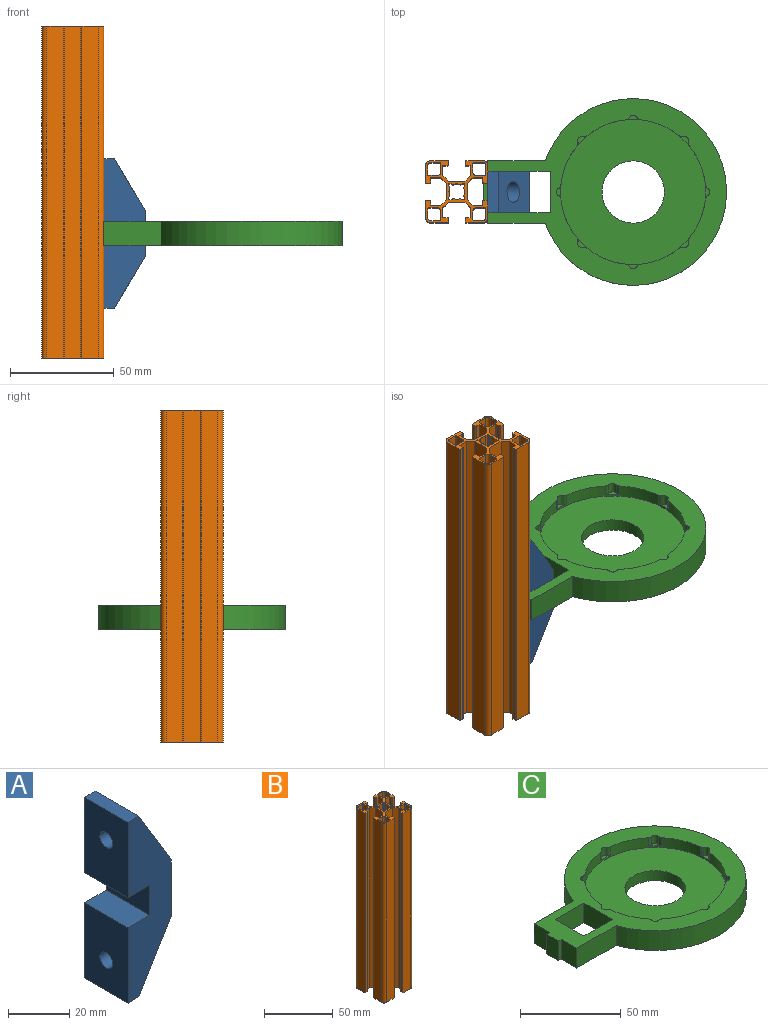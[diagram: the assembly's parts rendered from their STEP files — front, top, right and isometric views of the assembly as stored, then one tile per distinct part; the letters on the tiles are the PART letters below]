
ASSEMBLY  parts=3 mates=2
PART A: 18 faces, bbox 20x20x72 mm
  f0: cylinder r=3mm len=6.8mm, axis (1,0,0), area 128.1mm2, adj f4,f10
  f1: plane 72x20mm, normal (0,1,0), area 945mm2, adj f2,f3,f4,f5,f6,f7,f12,f13
  f2: plane 25x20mm, normal (0.86,0,0.51), area 491.5mm2, adj f1,f3,f7,f8,f9
  f3: plane 20x5mm, normal (0,0,1), area 100mm2, adj f1,f2,f4,f8
  f4: plane 30x20mm, normal (-1,0,0), area 571.7mm2, adj f0,f1,f3,f5,f8
  f5: plane 20x10mm, normal (0,0,-1), area 200mm2, adj f1,f4,f6,f8
  f6: plane 20x12mm, normal (-1,0,0), area 240mm2, adj f1,f5,f8,f15
  f7: plane 22x20mm, normal (1,0,0), area 440mm2, adj f1,f2,f8,f12
  f8: plane 72x20mm, normal (0,-1,0), area 945mm2, adj f2,f3,f4,f5,f6,f7,f12,f13
  f9: cylinder r=5mm len=10mm, axis (1,0,0), area 131.9mm2, adj f2,f10
  f10: cone r=0mm half-angle=59deg, axis (1,0,0), area 58.6mm2, adj f0,f9
  f11: cylinder r=3mm len=6.8mm, axis (1,0,0), area 128.1mm2, adj f14,f17
  f12: plane 25x20mm, normal (0.86,0,-0.51), area 491.5mm2, adj f1,f7,f8,f13,f16
  f13: plane 20x5mm, normal (0,0,-1), area 100mm2, adj f1,f8,f12,f14
  f14: plane 30x20mm, normal (-1,0,0), area 571.7mm2, adj f1,f8,f11,f13,f15
  f15: plane 20x10mm, normal (0,0,1), area 200mm2, adj f1,f6,f8,f14
  f16: cylinder r=5mm len=10mm, axis (1,0,0), area 131.9mm2, adj f12,f17
  f17: cone r=0mm half-angle=59deg, axis (1,0,0), area 58.6mm2, adj f11,f16
PART B: 138 faces, bbox 30x30x160 mm
  f0: cylinder r=0.5mm len=160mm, axis (0,0,-1), area 125.7mm2, adj f1,f135,f136,f137
  f1: plane 160x4.2mm, normal (0,-1,0), area 672mm2, adj f0,f2,f136,f137
  f2: cylinder r=1.5mm len=160mm, axis (0,0,-1), area 377mm2, adj f1,f3,f136,f137
  f3: plane 160x4.2mm, normal (-1,0,0), area 672mm2, adj f2,f4,f136,f137
  f4: cylinder r=0.5mm len=160mm, axis (0,0,-1), area 125.7mm2, adj f3,f5,f136,f137
  f5: plane 160x4.2mm, normal (0,1,0), area 672mm2, adj f4,f6,f136,f137
  f6: cylinder r=1.5mm len=160mm, axis (0,0,-1), area 377mm2, adj f5,f135,f136,f137
  f7: cylinder r=1.5mm len=160mm, axis (0,0,-1), area 377mm2, adj f8,f130,f136,f137
  f8: plane 160x4.2mm, normal (0,-1,0), area 672mm2, adj f7,f9,f136,f137
  f9: cylinder r=0.5mm len=160mm, axis (0,0,-1), area 125.7mm2, adj f8,f10,f136,f137
  f10: plane 160x4.2mm, normal (-1,0,0), area 672mm2, adj f9,f11,f136,f137
  f11: cylinder r=1.5mm len=160mm, axis (0,0,-1), area 377mm2, adj f10,f12,f136,f137
  f12: plane 160x4.2mm, normal (0,1,0), area 672mm2, adj f11,f13,f136,f137
  f13: cylinder r=0.5mm len=160mm, axis (0,0,-1), area 125.7mm2, adj f12,f130,f136,f137
  f14: cylinder r=0.5mm len=160mm, axis (0,0,-1), area 125.7mm2, adj f15,f131,f136,f137
  f15: plane 160x4.2mm, normal (0,-1,0), area 672mm2, adj f14,f16,f136,f137
  f16: cylinder r=1.5mm len=160mm, axis (0,0,-1), area 377mm2, adj f15,f17,f136,f137
  f17: plane 160x4.2mm, normal (-1,0,0), area 672mm2, adj f16,f18,f136,f137
  f18: cylinder r=0.5mm len=160mm, axis (0,0,-1), area 125.7mm2, adj f17,f19,f136,f137
  f19: plane 160x4.2mm, normal (0,1,0), area 672mm2, adj f18,f20,f136,f137
  f20: cylinder r=1.5mm len=160mm, axis (0,0,-1), area 377mm2, adj f19,f131,f136,f137
  f21: cylinder r=1.5mm len=160mm, axis (0,0,-1), area 377mm2, adj f22,f132,f136,f137
  f22: plane 160x4.2mm, normal (0,-1,0), area 672mm2, adj f21,f23,f136,f137
  f23: cylinder r=0.5mm len=160mm, axis (0,0,-1), area 125.7mm2, adj f22,f24,f136,f137
  f24: plane 160x4.2mm, normal (-1,0,0), area 672mm2, adj f23,f25,f136,f137
  f25: cylinder r=1.5mm len=160mm, axis (0,0,-1), area 377mm2, adj f24,f26,f136,f137
  f26: plane 160x4.2mm, normal (0,1,0), area 672mm2, adj f25,f27,f136,f137
  f27: cylinder r=0.5mm len=160mm, axis (0,0,-1), area 125.7mm2, adj f26,f132,f136,f137
  f28: plane 160x0.24mm, normal (0.71,-0.71,0), area 53.8mm2, adj f29,f133,f136,f137
  f29: cylinder r=0.3mm len=160mm, axis (0,0,-1), area 59.7mm2, adj f28,f30,f136,f137
  f30: cylinder r=3.75mm len=160mm, axis (0,0,-1), area 550.4mm2, adj f29,f31,f136,f137
  f31: cylinder r=0.3mm len=160mm, axis (0,0,-1), area 59.7mm2, adj f30,f32,f136,f137
  f32: plane 160x0.24mm, normal (0.71,0.71,0), area 53.8mm2, adj f31,f33,f136,f137
  f33: plane 160x1.04mm, normal (0.98,0.21,0), area 170.6mm2, adj f32,f34,f136,f137
  f34: cylinder r=0.5mm len=160mm, axis (0,0,-1), area 159.2mm2, adj f33,f35,f136,f137
  f35: plane 160x1.04mm, normal (-0.21,-0.98,0), area 170.6mm2, adj f34,f36,f136,f137
  f36: plane 160x0.24mm, normal (-0.71,-0.71,0), area 53.8mm2, adj f35,f37,f136,f137
  f37: cylinder r=0.3mm len=160mm, axis (0,0,-1), area 59.7mm2, adj f36,f38,f136,f137
  f38: cylinder r=3.75mm len=160mm, axis (0,0,-1), area 550.4mm2, adj f37,f39,f136,f137
  f39: cylinder r=0.3mm len=160mm, axis (0,0,-1), area 59.7mm2, adj f38,f40,f136,f137
  f40: plane 160x0.24mm, normal (0.71,-0.71,0), area 53.8mm2, adj f39,f41,f136,f137
  f41: plane 160x1.04mm, normal (0.21,-0.98,0), area 170.6mm2, adj f40,f42,f136,f137
  f42: cylinder r=0.5mm len=160mm, axis (0,0,-1), area 159.2mm2, adj f41,f43,f136,f137
  f43: plane 160x1.04mm, normal (-0.98,0.21,0), area 170.6mm2, adj f42,f44,f136,f137
  f44: plane 160x0.24mm, normal (-0.71,0.71,0), area 53.8mm2, adj f43,f45,f136,f137
  f45: cylinder r=0.3mm len=160mm, axis (0,0,-1), area 59.7mm2, adj f44,f46,f136,f137
  f46: cylinder r=3.75mm len=160mm, axis (0,0,-1), area 550.4mm2, adj f45,f47,f136,f137
  f47: cylinder r=0.3mm len=160mm, axis (0,0,-1), area 59.7mm2, adj f46,f48,f136,f137
  f48: plane 160x0.24mm, normal (-0.71,-0.71,0), area 53.8mm2, adj f47,f49,f136,f137
  f49: plane 160x1.04mm, normal (-0.98,-0.21,0), area 170.6mm2, adj f48,f50,f136,f137
  f50: cylinder r=0.5mm len=160mm, axis (0,0,-1), area 159.2mm2, adj f49,f51,f136,f137
  f51: plane 160x1.04mm, normal (0.21,0.98,0), area 170.6mm2, adj f50,f52,f136,f137
  f52: plane 160x0.24mm, normal (0.71,0.71,0), area 53.8mm2, adj f51,f53,f136,f137
  f53: cylinder r=0.3mm len=160mm, axis (0,0,-1), area 59.7mm2, adj f52,f54,f136,f137
  f54: cylinder r=3.75mm len=160mm, axis (0,0,-1), area 550.4mm2, adj f53,f55,f136,f137
  f55: cylinder r=0.3mm len=160mm, axis (0,0,-1), area 59.7mm2, adj f54,f56,f136,f137
  f56: plane 160x0.24mm, normal (-0.71,0.71,0), area 53.8mm2, adj f55,f57,f136,f137
  f57: plane 160x1.04mm, normal (-0.21,0.98,0), area 170.6mm2, adj f56,f58,f136,f137
  f58: cylinder r=0.5mm len=160mm, axis (0,0,-1), area 159.2mm2, adj f57,f133,f136,f137
  f59: cylinder r=0.3mm len=160mm, axis (0,0,-1), area 75.4mm2, adj f60,f134,f136,f137
  f60: plane 160x4.34mm, normal (-1,0,0), area 694.3mm2, adj f59,f61,f136,f137
  f61: plane 160x2.86mm, normal (-0.71,0.71,0), area 647.3mm2, adj f60,f62,f136,f137
  f62: plane 160x7.88mm, normal (0,1,0), area 1260.6mm2, adj f61,f63,f136,f137
  f63: plane 160x2.86mm, normal (0.71,0.71,0), area 647.3mm2, adj f62,f64,f136,f137
  f64: plane 160x4.34mm, normal (1,0,0), area 694.3mm2, adj f63,f65,f136,f137
  f65: cylinder r=0.3mm len=160mm, axis (0,0,-1), area 75.4mm2, adj f64,f66,f136,f137
  f66: plane 160x1.9mm, normal (0,-1,0), area 304mm2, adj f65,f67,f136,f137
  f67: cylinder r=0.5mm len=160mm, axis (0,0,-1), area 125.7mm2, adj f66,f68,f136,f137
  f68: plane 160x1.7mm, normal (1,0,0), area 272mm2, adj f67,f69,f136,f137
  f69: cylinder r=0.3mm len=160mm, axis (0,0,-1), area 75.4mm2, adj f68,f70,f136,f137
  f70: plane 160x8.1mm, normal (0,1,0), area 1296mm2, adj f69,f71,f136,f137
  f71: cylinder r=2.5mm len=160mm, axis (0,0,-1), area 628.3mm2, adj f70,f72,f136,f137
  f72: plane 160x8.1mm, normal (-1,0,0), area 1296mm2, adj f71,f73,f136,f137
  f73: cylinder r=0.3mm len=160mm, axis (0,0,-1), area 75.4mm2, adj f72,f74,f136,f137
  f74: plane 160x1.7mm, normal (0,-1,0), area 272mm2, adj f73,f75,f136,f137
  f75: cylinder r=0.5mm len=160mm, axis (0,0,-1), area 125.7mm2, adj f74,f76,f136,f137
  f76: plane 160x1.9mm, normal (1,0,0), area 304mm2, adj f75,f77,f136,f137
  f77: cylinder r=0.3mm len=160mm, axis (0,0,-1), area 75.4mm2, adj f76,f78,f136,f137
  f78: plane 160x4.34mm, normal (0,-1,0), area 694.3mm2, adj f77,f79,f136,f137
  f79: plane 160x2.86mm, normal (-0.71,-0.71,0), area 647.3mm2, adj f78,f80,f136,f137
  f80: plane 160x7.88mm, normal (-1,0,0), area 1260.6mm2, adj f79,f81,f136,f137
  f81: plane 160x2.86mm, normal (-0.71,0.71,0), area 647.3mm2, adj f80,f82,f136,f137
  f82: plane 160x4.34mm, normal (0,1,0), area 694.3mm2, adj f81,f83,f136,f137
  f83: cylinder r=0.3mm len=160mm, axis (0,0,-1), area 75.4mm2, adj f82,f84,f136,f137
  f84: plane 160x1.9mm, normal (1,0,0), area 304mm2, adj f83,f85,f136,f137
  f85: cylinder r=0.5mm len=160mm, axis (0,0,-1), area 125.7mm2, adj f84,f86,f136,f137
  f86: plane 160x1.7mm, normal (0,1,0), area 272mm2, adj f85,f87,f136,f137
  f87: cylinder r=0.3mm len=160mm, axis (0,0,-1), area 75.4mm2, adj f86,f88,f136,f137
  f88: plane 160x8.1mm, normal (-1,0,0), area 1296mm2, adj f87,f89,f136,f137
  f89: cylinder r=2.5mm len=160mm, axis (0,0,-1), area 628.3mm2, adj f88,f90,f136,f137
  f90: plane 160x8.1mm, normal (0,-1,0), area 1296mm2, adj f89,f91,f136,f137
  f91: cylinder r=0.3mm len=160mm, axis (0,0,-1), area 75.4mm2, adj f90,f92,f136,f137
  f92: plane 160x1.7mm, normal (1,0,0), area 272mm2, adj f91,f93,f136,f137
  f93: cylinder r=0.5mm len=160mm, axis (0,0,-1), area 125.7mm2, adj f92,f94,f136,f137
  f94: plane 160x1.9mm, normal (0,1,0), area 304mm2, adj f93,f95,f136,f137
  f95: cylinder r=0.3mm len=160mm, axis (0,0,-1), area 75.4mm2, adj f94,f96,f136,f137
  f96: plane 160x4.34mm, normal (1,0,0), area 694.3mm2, adj f95,f97,f136,f137
  f97: plane 160x2.86mm, normal (0.71,-0.71,0), area 647.3mm2, adj f96,f98,f136,f137
  f98: plane 160x7.88mm, normal (0,-1,0), area 1260.6mm2, adj f97,f99,f136,f137
  f99: plane 160x2.86mm, normal (-0.71,-0.71,0), area 647.3mm2, adj f98,f100,f136,f137
  f100: plane 160x4.34mm, normal (-1,0,0), area 694.3mm2, adj f99,f101,f136,f137
  f101: cylinder r=0.3mm len=160mm, axis (0,0,-1), area 75.4mm2, adj f100,f102,f136,f137
  f102: plane 160x1.9mm, normal (0,1,0), area 304mm2, adj f101,f103,f136,f137
  f103: cylinder r=0.5mm len=160mm, axis (0,0,-1), area 125.7mm2, adj f102,f104,f136,f137
  f104: plane 160x1.7mm, normal (-1,0,0), area 272mm2, adj f103,f105,f136,f137
  f105: cylinder r=0.3mm len=160mm, axis (0,0,-1), area 75.4mm2, adj f104,f106,f136,f137
  f106: plane 160x8.1mm, normal (0,-1,0), area 1296mm2, adj f105,f107,f136,f137
  f107: cylinder r=2.5mm len=160mm, axis (0,0,-1), area 628.3mm2, adj f106,f108,f136,f137
  f108: plane 160x8.1mm, normal (1,0,0), area 1296mm2, adj f107,f109,f136,f137
  f109: cylinder r=0.3mm len=160mm, axis (0,0,-1), area 75.4mm2, adj f108,f110,f136,f137
  f110: plane 160x1.7mm, normal (0,1,0), area 272mm2, adj f109,f111,f136,f137
  f111: cylinder r=0.5mm len=160mm, axis (0,0,-1), area 125.7mm2, adj f110,f112,f136,f137
  f112: plane 160x1.9mm, normal (-1,0,0), area 304mm2, adj f111,f113,f136,f137
  f113: cylinder r=0.3mm len=160mm, axis (0,0,-1), area 75.4mm2, adj f112,f114,f136,f137
  f114: plane 160x4.34mm, normal (0,1,0), area 694.3mm2, adj f113,f115,f136,f137
  f115: plane 160x2.86mm, normal (0.71,0.71,0), area 647.3mm2, adj f114,f116,f136,f137
  f116: plane 160x7.88mm, normal (1,0,0), area 1260.6mm2, adj f115,f117,f136,f137
  f117: plane 160x2.86mm, normal (0.71,-0.71,0), area 647.3mm2, adj f116,f118,f136,f137
  f118: plane 160x4.34mm, normal (0,-1,0), area 694.3mm2, adj f117,f119,f136,f137
  f119: cylinder r=0.3mm len=160mm, axis (0,0,-1), area 75.4mm2, adj f118,f120,f136,f137
  f120: plane 160x1.9mm, normal (-1,0,0), area 304mm2, adj f119,f121,f136,f137
  f121: cylinder r=0.5mm len=160mm, axis (0,0,-1), area 125.7mm2, adj f120,f122,f136,f137
  f122: plane 160x1.7mm, normal (0,-1,0), area 272mm2, adj f121,f123,f136,f137
  f123: cylinder r=0.3mm len=160mm, axis (0,0,-1), area 75.4mm2, adj f122,f124,f136,f137
  f124: plane 160x8.1mm, normal (1,0,0), area 1296mm2, adj f123,f125,f136,f137
  f125: cylinder r=2.5mm len=160mm, axis (0,0,-1), area 628.3mm2, adj f124,f126,f136,f137
  f126: plane 160x8.1mm, normal (0,1,0), area 1296mm2, adj f125,f127,f136,f137
  f127: cylinder r=0.3mm len=160mm, axis (0,0,-1), area 75.4mm2, adj f126,f128,f136,f137
  f128: plane 160x1.7mm, normal (-1,0,0), area 272mm2, adj f127,f129,f136,f137
  f129: cylinder r=0.5mm len=160mm, axis (0,0,-1), area 125.7mm2, adj f128,f134,f136,f137
  f130: plane 160x4.2mm, normal (1,0,0), area 672mm2, adj f7,f13,f136,f137
  f131: plane 160x4.2mm, normal (1,0,0), area 672mm2, adj f14,f20,f136,f137
  f132: plane 160x4.2mm, normal (1,0,0), area 672mm2, adj f21,f27,f136,f137
  f133: plane 160x1.04mm, normal (0.98,-0.21,0), area 170.6mm2, adj f28,f58,f136,f137
  f134: plane 160x1.9mm, normal (0,-1,0), area 304mm2, adj f59,f129,f136,f137
  f135: plane 160x4.2mm, normal (1,0,0), area 672mm2, adj f0,f6,f136,f137
  f136: plane 30x30mm, normal (0,0,1), area 233.9mm2, adj f0,f1,f2,f3,f4,f5,f6,f7
  f137: plane 30x30mm, normal (0,0,-1), area 233.9mm2, adj f0,f1,f2,f3,f4,f5,f6,f7
PART C: 49 faces, bbox 117x90x12 mm
  f0: plane 12x10.9mm, normal (-1,0,0), area 130.8mm2, adj f1,f2,f7,f46
  f1: plane 117x90mm, normal (0,0,-1), area 6046.7mm2, adj f0,f3,f6,f7,f8,f9,f42,f43
  f2: plane 117x90mm, normal (0,0,1), area 2849.6mm2, adj f0,f5,f6,f7,f8,f9,f10,f12
  f3: cylinder r=15mm len=30mm, axis (0,0,-1), area 565.5mm2, adj f1,f4
  f4: plane 70x70mm, normal (0,0,1), area 3141.6mm2, adj f3,f5
  f5: cylinder r=35mm len=70mm, axis (0,0,-1), area 1049.8mm2, adj f2,f4,f11,f12,f13,f15,f16,f17
  f6: cylinder r=45mm len=90mm, axis (0,0,-1), area 3025.9mm2, adj f1,f2,f7,f9
  f7: plane 27.57x12mm, normal (0,1,0), area 330.9mm2, adj f0,f1,f2,f6
  f8: plane 12x10.9mm, normal (-1,0,0), area 130.8mm2, adj f1,f2,f9,f47
  f9: plane 27.57x12mm, normal (0,-1,0), area 330.9mm2, adj f1,f2,f6,f8
  f10: cylinder r=2mm len=5mm, axis (0,0,1), area 21.9mm2, adj f2,f11,f12,f13
  f11: plane 6.73x2.16mm, normal (0,0,1), area 6.9mm2, adj f5,f10,f12,f13
  f12: cylinder r=2mm len=5mm, axis (0,0,1), area 10mm2, adj f2,f5,f10,f11
  f13: cylinder r=2mm len=5mm, axis (0,0,-1), area 10mm2, adj f2,f5,f10,f11
  f14: cylinder r=2mm len=5mm, axis (0,0,1), area 21.9mm2, adj f2,f15,f16,f17
  f15: plane 4.76x4.76mm, normal (0,0,1), area 6.9mm2, adj f5,f14,f16,f17
  f16: cylinder r=2mm len=5mm, axis (0,0,1), area 10mm2, adj f2,f5,f14,f15
  f17: cylinder r=2mm len=5mm, axis (0,0,-1), area 10mm2, adj f2,f5,f14,f15
  f18: cylinder r=2mm len=5mm, axis (0,0,1), area 21.9mm2, adj f2,f19,f20,f21
  f19: plane 6.73x2.16mm, normal (0,0,1), area 6.9mm2, adj f5,f18,f20,f21
  f20: cylinder r=2mm len=5mm, axis (0,0,1), area 10mm2, adj f2,f5,f18,f19
  f21: cylinder r=2mm len=5mm, axis (0,0,-1), area 10mm2, adj f2,f5,f18,f19
  f22: cylinder r=2mm len=5mm, axis (0,0,1), area 21.9mm2, adj f2,f23,f24,f25
  f23: plane 4.76x4.76mm, normal (0,0,1), area 6.9mm2, adj f5,f22,f24,f25
  f24: cylinder r=2mm len=5mm, axis (0,0,1), area 10mm2, adj f2,f5,f22,f23
  f25: cylinder r=2mm len=5mm, axis (0,0,-1), area 10mm2, adj f2,f5,f22,f23
  f26: cylinder r=2mm len=5mm, axis (0,0,1), area 21.9mm2, adj f2,f27,f28,f29
  f27: plane 6.73x2.16mm, normal (0,0,1), area 6.9mm2, adj f5,f26,f28,f29
  f28: cylinder r=2mm len=5mm, axis (0,0,1), area 10mm2, adj f2,f5,f26,f27
  f29: cylinder r=2mm len=5mm, axis (0,0,-1), area 10mm2, adj f2,f5,f26,f27
  f30: cylinder r=2mm len=5mm, axis (0,0,1), area 21.9mm2, adj f2,f31,f32,f33
  f31: plane 4.76x4.76mm, normal (0,0,1), area 6.9mm2, adj f5,f30,f32,f33
  f32: cylinder r=2mm len=5mm, axis (0,0,1), area 10mm2, adj f2,f5,f30,f31
  f33: cylinder r=2mm len=5mm, axis (0,0,-1), area 10mm2, adj f2,f5,f30,f31
  f34: cylinder r=2mm len=5mm, axis (0,0,1), area 21.9mm2, adj f2,f35,f36,f37
  f35: plane 6.73x2.16mm, normal (0,0,1), area 6.9mm2, adj f5,f34,f36,f37
  f36: cylinder r=2mm len=5mm, axis (0,0,1), area 10mm2, adj f2,f5,f34,f35
  f37: cylinder r=2mm len=5mm, axis (0,0,-1), area 10mm2, adj f2,f5,f34,f35
  f38: cylinder r=2mm len=5mm, axis (0,0,1), area 21.9mm2, adj f2,f39,f40,f41
  f39: plane 4.76x4.76mm, normal (0,0,1), area 6.9mm2, adj f5,f38,f40,f41
  f40: cylinder r=2mm len=5mm, axis (0,0,1), area 10mm2, adj f2,f5,f38,f39
  f41: cylinder r=2mm len=5mm, axis (0,0,-1), area 10mm2, adj f2,f5,f38,f39
  f42: plane 20x12mm, normal (-1,0,0), area 240mm2, adj f1,f2,f43,f44
  f43: plane 20x12mm, normal (0,-1,0), area 240mm2, adj f1,f2,f42,f45
  f44: plane 20x12mm, normal (0,1,0), area 240mm2, adj f1,f2,f42,f45
  f45: plane 20x12mm, normal (1,0,0), area 240mm2, adj f1,f2,f43,f44
  f46: plane 12x2mm, normal (0,1,0), area 24mm2, adj f0,f1,f2,f48
  f47: plane 12x2mm, normal (0,-1,0), area 24mm2, adj f1,f2,f8,f48
  f48: plane 12x8.2mm, normal (-1,0,0), area 98.4mm2, adj f1,f2,f46,f47
PLACE A t=(13.47,-10.24,40.59)mm
PLACE B t=(-71.53,-10.24,-13.41)mm fixed
PLACE C t=(13.47,-10.24,40.59)mm
MATE fastened B.f108 <-> C.f8  axis (-1,0,0) through (-56.53,-10.24,46.59)mm
MATE fastened A.f6 <-> C.f45  axis (-1,0,0) through (-46.53,-10.24,46.59)mm
